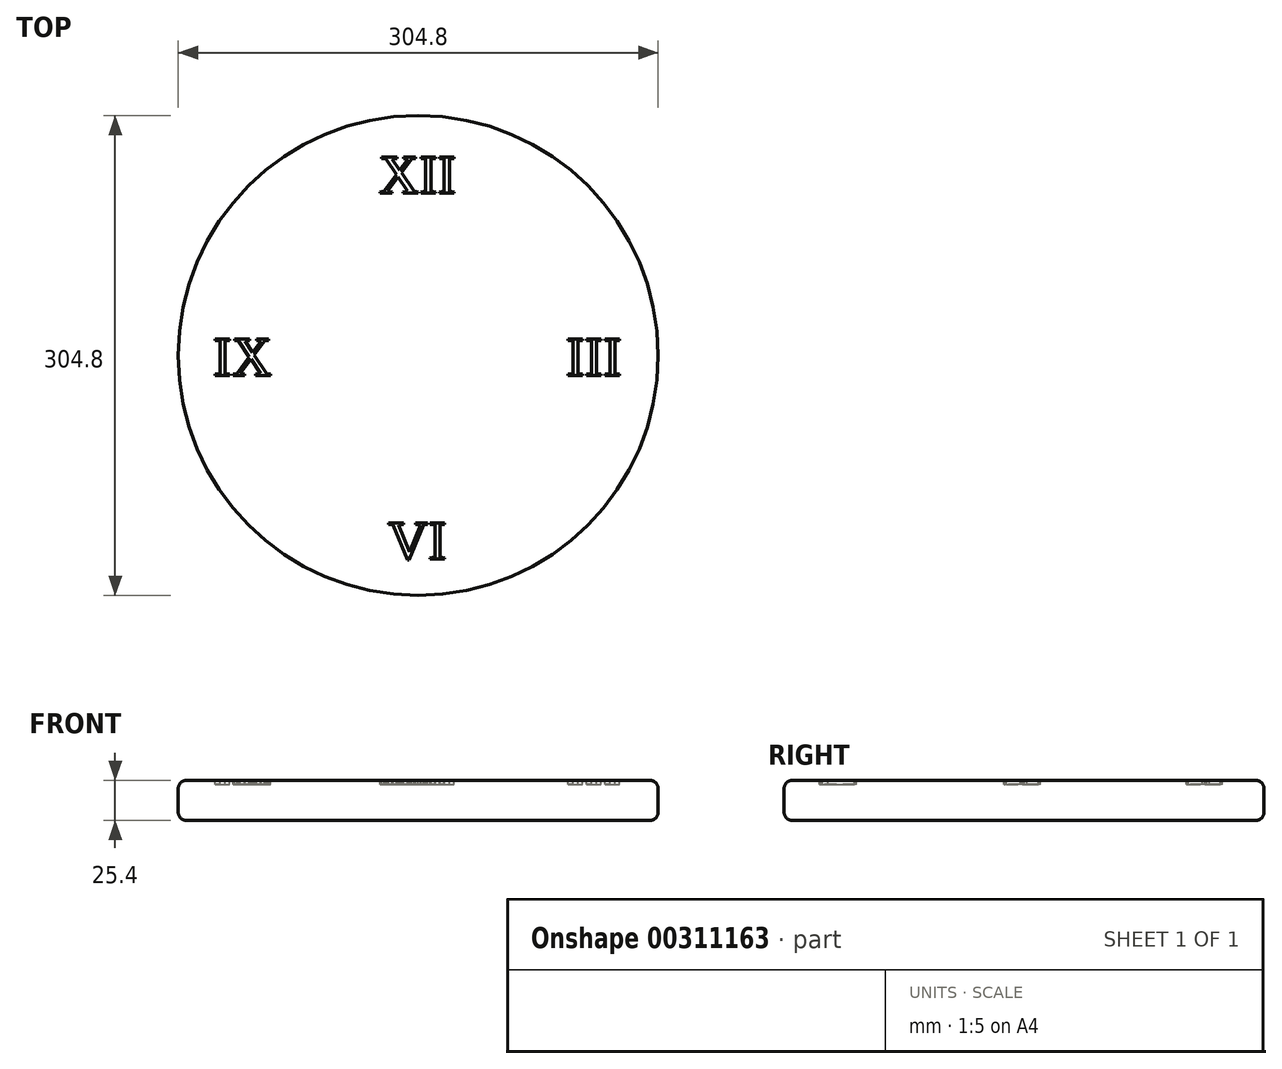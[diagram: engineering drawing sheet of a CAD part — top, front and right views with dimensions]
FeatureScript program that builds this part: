
annotation { "Feature Type Name" : "Feature", "Feature Type Description" : "" }
export const myFeature = defineFeature(function(context is Context, id is Id, definition is map)
    precondition{}
    {
        {
            var Q0;
            Q0=qCreatedBy(makeId("Top.planeOp"),FACE);
            var sketch = newSketch(context, id + "F0", { "sketchPlane" : qUnion([Q0])});
            skCircle(sketch, "E0", {"center": v(0, 0) * mm, "radius": 152.4 * mm});
            skSolve(sketch);
        }
        {
            var Q0;
            Q0 = qSketchRegion(id + "F0", true);
            extrude(context, id + "F1", {"entities" : qUnion([Q0]), "depth" : 25.4 * mm});
        }
        {
            var Q0;
            Q0=makeQuery(id+"F1.opExtrude","CAP_FACE",FACE,{"disambiguationData":[OSD([sQuery(id+"F0.wireOp",EDGE,"E0")])],"isStart":false});
            var Q1;
            Q1=makeQuery(id+"F1.opExtrude","CAP_EDGE",EDGE,{"disambiguationData":[OSD([sQuery(id+"F0.wireOp",EDGE,"E0")])],"isStart":true});
            fillet(context, id + "F2", {"entities" : qUnion([Q0, Q1]), "radius" : 5.08 * mm, "tangentPropagation" : true, "allowEdgeOverflow" : false});
        }
        {
            var Q0;
            Q0=makeQuery(id+"F1.opExtrude","CAP_FACE",FACE,{"disambiguationData":[OSD([sQuery(id+"F0.wireOp",EDGE,"E0")])],"isStart":false});
            var sketch = newSketch(context, id + "F3", { "sketchPlane" : qUnion([Q0])});
            skText(sketch, "E1", { "text": "XII", "fontName": "Tinos-Regular.ttf"});
            skLineSegment(sketch, "E2", {"start": v(0, 128.4) * mm, "end": v(0, 147.32) * mm, "construction": true});
            skCircle(sketch, "E3", {"center": v(0, 0) * mm, "radius": 130.8 * mm, "construction": true});
            skText(sketch, "E4", { "text": "III", "fontName": "Tinos-Regular.ttf"});
            skLineSegment(sketch, "E5", {"start": v(130.2, 0) * mm, "end": v(130.8, 0) * mm, "construction": true});
            skText(sketch, "E6", { "text": "VI", "fontName": "Tinos-Regular.ttf"});
            skLineSegment(sketch, "E7", {"start": v(0, -129.4) * mm, "end": v(0, -130.8) * mm, "construction": true});
            skText(sketch, "E8", { "text": "IX", "fontName": "Tinos-Regular.ttf"});
            skLineSegment(sketch, "E9", {"start": v(-130.2, 0) * mm, "end": v(-130.8, 0) * mm, "construction": true});
            const initialGuessF3  = {"E1": [-0.02497, 0.103, 1, 0, 0.0254], "E4": [0.09399, -0.0127, 1, 0, 0.0254], "E6": [-0.0191, -0.1294, 1, 0, 0.0254], "E8": [-0.1302, -0.0127, 1, 0, 0.0254]};
            skSetInitialGuess(sketch, initialGuessF3);
            skSolve(sketch);
        }
        {
            var Q0;
            Q0 = qSketchRegion(id + "F3", true);
            extrude(context, id + "F4", {"entities" : qUnion([Q0]), "operationType" : NewBodyOperationType.REMOVE, "oppositeDirection" : true, "depth" : 2.54 * mm});
        }
    });
